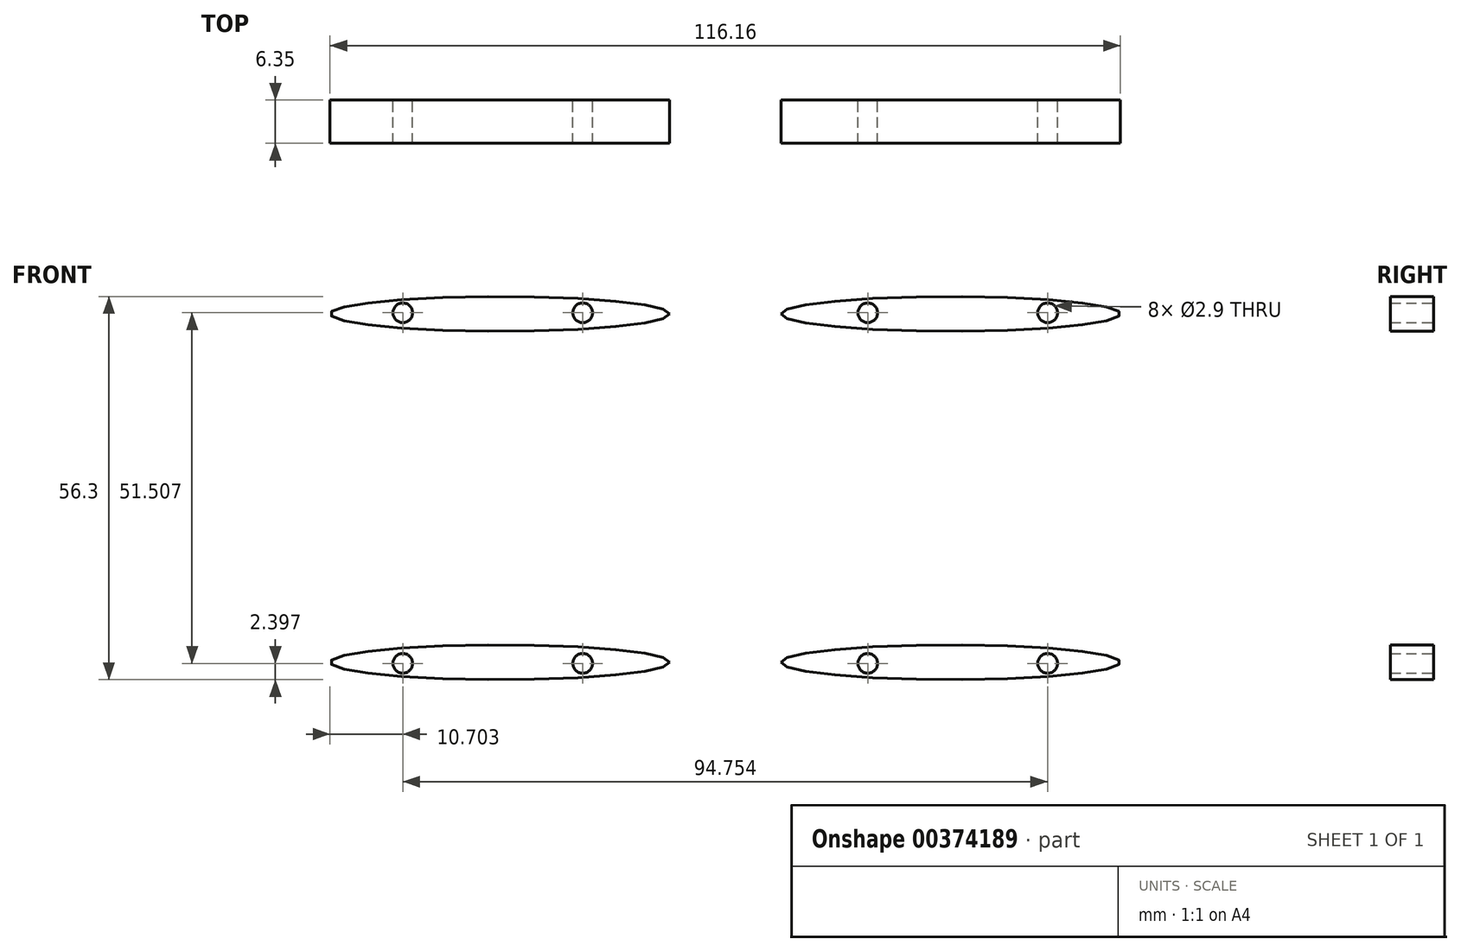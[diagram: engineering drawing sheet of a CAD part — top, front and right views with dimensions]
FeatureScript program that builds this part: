
annotation { "Feature Type Name" : "Feature", "Feature Type Description" : "" }
export const myFeature = defineFeature(function(context is Context, id is Id, definition is map)
    precondition{}
    {
        {
            var Q0;
            Q0=qCreatedBy(makeId("Front.planeOp"),FACE);
            var sketch = newSketch(context, id + "F0", { "sketchPlane" : qUnion([Q0])});
            skEllipse(sketch, "E0", {"center": v(-33.14, 25.6) * mm, "majorRadius": 24.94 * mm, "minorRadius": 2.55 * mm, "majorAxis": v(1, 0)});
            skCircle(sketch, "E1", {"center": v(-47.38, 25.75) * mm, "radius": 1.45 * mm});
            skCircle(sketch, "E2", {"center": v(-20.94, 25.75) * mm, "radius": 1.45 * mm});
            skLineSegment(sketch, "E3", {"start": v(0, 76.73) * mm, "end": v(0, -75.12) * mm});
            skLineSegment(sketch, "E4", {"start": v(-76.14, 0) * mm, "end": v(76.1, 0) * mm});
            skCircle(sketch, "E5.MirrorC", {"center": v(20.94, 25.75) * mm, "radius": 1.45 * mm});
            skCircle(sketch, "E6.MirrorC", {"center": v(47.38, 25.75) * mm, "radius": 1.45 * mm});
            skEllipse(sketch, "E7.MirrorC", {"center": v(33.14, 25.6) * mm, "majorRadius": 24.94 * mm, "minorRadius": 2.55 * mm, "majorAxis": v(-1, 0)});
            skCircle(sketch, "E8.MirrorC", {"center": v(-20.94, -25.75) * mm, "radius": 1.45 * mm});
            skCircle(sketch, "E9.MirrorC", {"center": v(-47.38, -25.75) * mm, "radius": 1.45 * mm});
            skEllipse(sketch, "E10.MirrorC", {"center": v(-33.14, -25.6) * mm, "majorRadius": 24.94 * mm, "minorRadius": 2.55 * mm, "majorAxis": v(1, 0)});
            skCircle(sketch, "E11.MirrorC", {"center": v(20.94, -25.75) * mm, "radius": 1.45 * mm});
            skEllipse(sketch, "E12.MirrorC", {"center": v(33.14, -25.6) * mm, "majorRadius": 24.94 * mm, "minorRadius": 2.55 * mm, "majorAxis": v(-1, 0)});
            skCircle(sketch, "E13.MirrorC", {"center": v(47.38, -25.75) * mm, "radius": 1.45 * mm});
            skSolve(sketch);
        }
        {
            var Q0;
            Q0=qSketchRegion(id+"F0",true);
            extrude(context, id + "F1", {"entities" : qUnion([Q0]), "depth" : 6.35 * mm});
        }
    });
